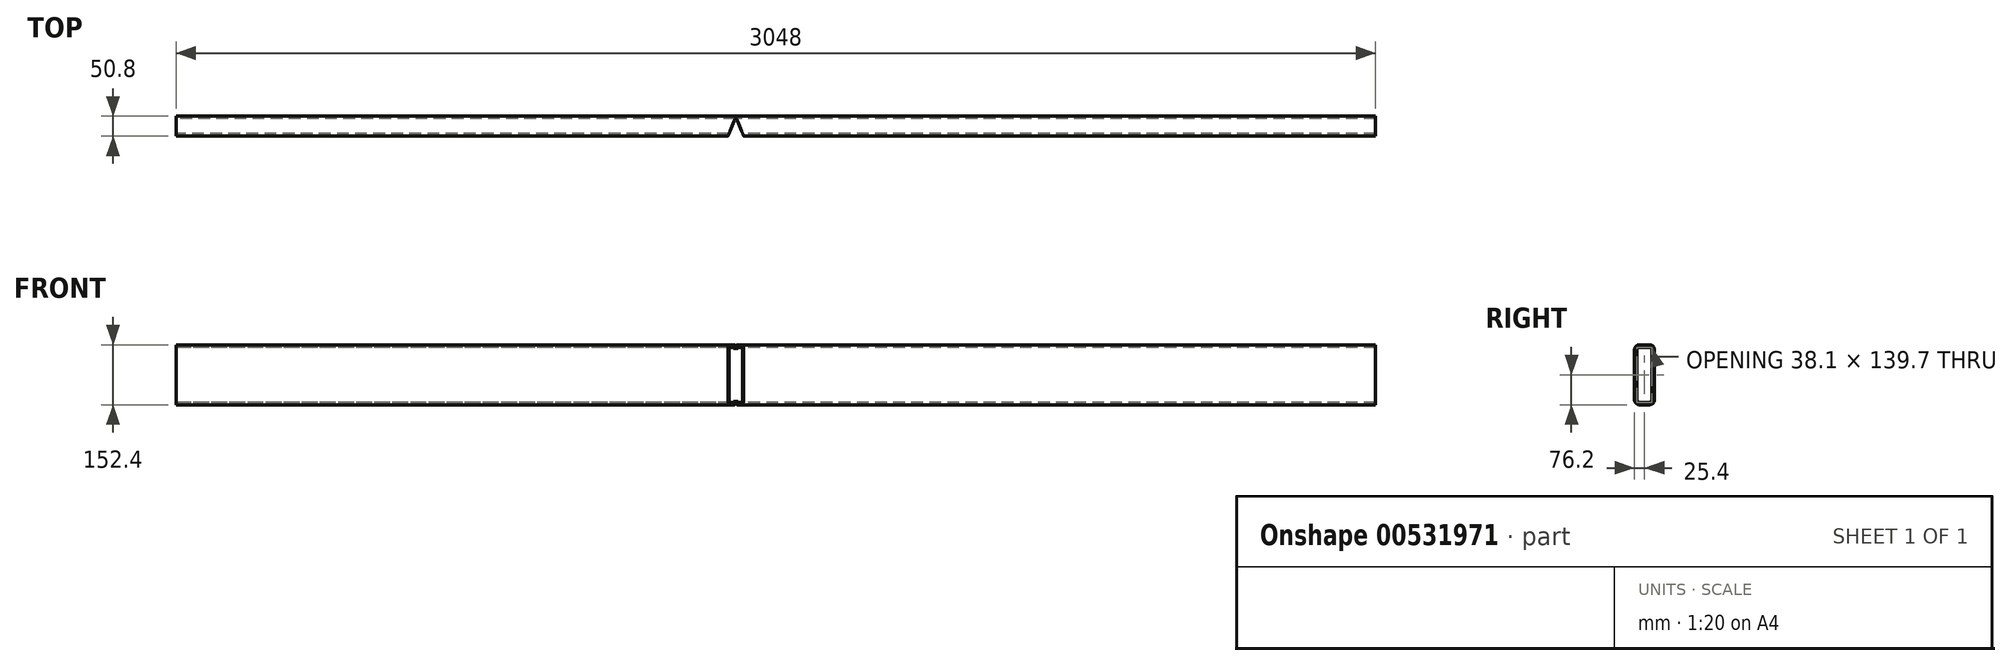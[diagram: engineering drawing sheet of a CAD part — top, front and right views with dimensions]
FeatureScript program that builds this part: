
annotation { "Feature Type Name" : "Feature", "Feature Type Description" : "" }
export const myFeature = defineFeature(function(context is Context, id is Id, definition is map)
    precondition{}
    {
        {
            var Q0;
            Q0=qCreatedBy(makeId("Right.planeOp"),FACE);
            var sketch = newSketch(context, id + "F0", { "sketchPlane" : qUnion([Q0])});
            skLineSegment(sketch, "E0.bottom", {"start": v(12.7, 76.2) * mm, "end": v(-12.7, 76.2) * mm});
            skLineSegment(sketch, "E0.top", {"start": v(12.7, -76.2) * mm, "end": v(-12.7, -76.2) * mm});
            skLineSegment(sketch, "E0.left", {"start": v(25.4, 63.5) * mm, "end": v(25.4, -63.5) * mm});
            skLineSegment(sketch, "E0.right", {"start": v(-25.4, 63.5) * mm, "end": v(-25.4, -63.5) * mm});
            skPoint(sketch, "E0.middle", {"position": v(0, 0) * mm});
            skLineSegment(sketch, "E1.0", {"start": v(-19.05, 63.5) * mm, "end": v(-19.05, -63.5) * mm});
            skLineSegment(sketch, "E1.1", {"start": v(12.7, 69.85) * mm, "end": v(-12.7, 69.85) * mm});
            skLineSegment(sketch, "E1.2", {"start": v(19.05, 63.5) * mm, "end": v(19.05, -63.5) * mm});
            skLineSegment(sketch, "E1.3", {"start": v(12.7, -69.85) * mm, "end": v(-12.7, -69.85) * mm});
            skPoint(sketch, "E2.visualSharp", {"position": v(-19.05, 69.85) * mm});
            skArc(sketch, "E2.filletArc", {"start": v(-12.7, 69.85) * mm, "mid": v(-17.2, 68) * mm, "end": v(-19.05, 63.5) * mm});
            skPoint(sketch, "E3.visualSharp", {"position": v(19.05, 69.85) * mm});
            skArc(sketch, "E3.filletArc", {"start": v(19.05, 63.5) * mm, "mid": v(17.2, 68) * mm, "end": v(12.7, 69.85) * mm});
            skPoint(sketch, "E4.visualSharp", {"position": v(19.05, -69.85) * mm});
            skArc(sketch, "E4.filletArc", {"start": v(12.7, -69.85) * mm, "mid": v(17.2, -68) * mm, "end": v(19.05, -63.5) * mm});
            skPoint(sketch, "E5.visualSharp", {"position": v(-19.05, -69.85) * mm});
            skArc(sketch, "E5.filletArc", {"start": v(-19.05, -63.5) * mm, "mid": v(-17.2, -68) * mm, "end": v(-12.7, -69.85) * mm});
            skPoint(sketch, "E6.visualSharp", {"position": v(-25.4, 76.2) * mm});
            skArc(sketch, "E6.filletArc", {"start": v(-12.7, 76.2) * mm, "mid": v(-21.68, 72.48) * mm, "end": v(-25.4, 63.5) * mm});
            skPoint(sketch, "E7.visualSharp", {"position": v(25.4, 76.2) * mm});
            skArc(sketch, "E7.filletArc", {"start": v(25.4, 63.5) * mm, "mid": v(21.68, 72.48) * mm, "end": v(12.7, 76.2) * mm});
            skPoint(sketch, "E8.visualSharp", {"position": v(25.4, -76.2) * mm});
            skArc(sketch, "E8.filletArc", {"start": v(12.7, -76.2) * mm, "mid": v(21.68, -72.48) * mm, "end": v(25.4, -63.5) * mm});
            skPoint(sketch, "E9.visualSharp", {"position": v(-25.4, -76.2) * mm});
            skArc(sketch, "E9.filletArc", {"start": v(-25.4, -63.5) * mm, "mid": v(-21.68, -72.48) * mm, "end": v(-12.7, -76.2) * mm});
            skSolve(sketch);
        }
        {
            var Q0;
            Q0=makeQuery(id+"F0.imprint","IMPRINT",FACE,{"disambiguationData":[TD([[makeQuery(id+"F0.imprint","IMPRINT",EDGE,{"derivedFrom":sQuery(id+"F0.wireOp",EDGE,"E0.bottom")}),1.0]])]});
            extrude(context, id + "F1", {"entities" : qUnion([Q0]), "depth" : 3048 * mm, "offsetDistance" : 25.4 * mm});
        }
        {
            var Q0;
            Q0=makeQuery(id+"F1.opExtrude","SWEPT_FACE",FACE,{"disambiguationData":[OSD([sQuery(id+"F0.wireOp",EDGE,"E0.bottom")])]});
            var sketch = newSketch(context, id + "F2", { "sketchPlane" : qUnion([Q0])});
            skLineSegment(sketch, "E10", {"start": v(1420.81, 19.05) * mm, "end": v(1402.4, -25.4) * mm});
            skLineSegment(sketch, "E11", {"start": v(1402.4, -25.4) * mm, "end": v(1442.4, -25.4) * mm});
            skLineSegment(sketch, "E12", {"start": v(1442.4, -25.4) * mm, "end": v(1423.99, 19.05) * mm});
            skLineSegment(sketch, "E13", {"start": v(1423.99, 19.05) * mm, "end": v(1420.81, 19.05) * mm});
            skPoint(sketch, "E14", {"position": v(1422.4, -25.4) * mm});
            skSolve(sketch);
        }
        {
            var Q0;
            Q0 = qSketchRegion(id + "F2", true);
            extrude(context, id + "F3", {"entities" : qUnion([Q0]), "operationType" : NewBodyOperationType.REMOVE, "endBound" : BoundingType.THROUGH_ALL, "oppositeDirection" : true, "depth" : 25.4 * mm, "offsetDistance" : 25.4 * mm});
        }
    });
